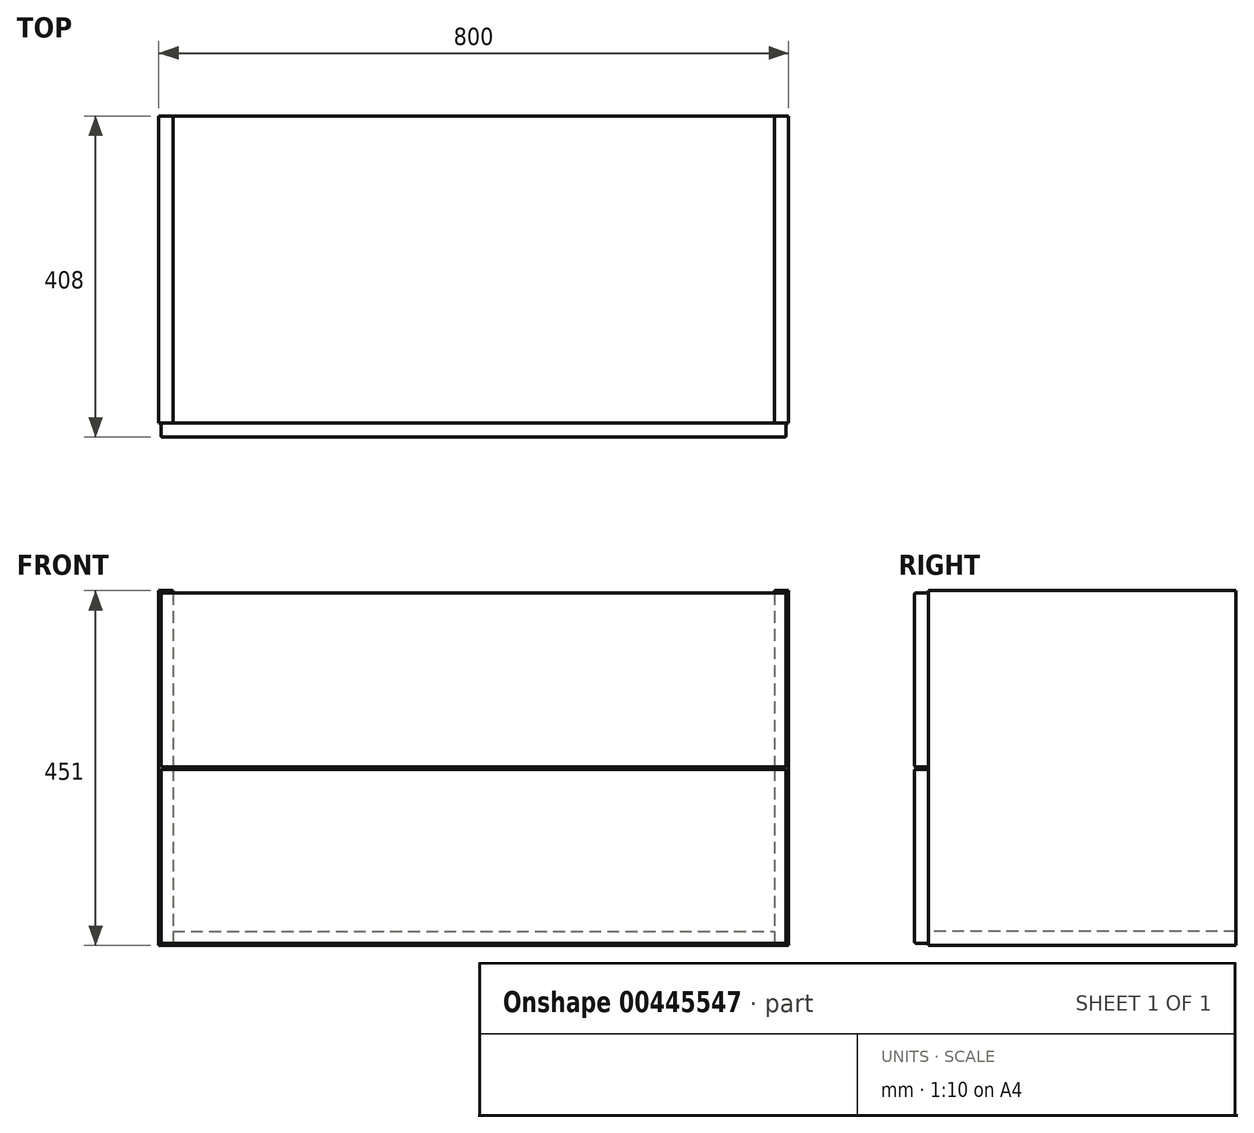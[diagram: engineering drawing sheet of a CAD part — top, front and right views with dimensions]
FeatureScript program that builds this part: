
annotation { "Feature Type Name" : "Feature", "Feature Type Description" : "" }
export const myFeature = defineFeature(function(context is Context, id is Id, definition is map)
    precondition{}
    {
        {
            var Q0;
            Q0=qCreatedBy(makeId("Front.planeOp"),FACE);
            var sketch = newSketch(context, id + "F0", { "sketchPlane" : qUnion([Q0])});
            skLineSegment(sketch, "E0.bottom", {"start": v(400, 225.5) * mm, "end": v(-400, 225.5) * mm});
            skLineSegment(sketch, "E0.top", {"start": v(400, -225.5) * mm, "end": v(-400, -225.5) * mm});
            skLineSegment(sketch, "E0.left", {"start": v(400, 225.5) * mm, "end": v(400, -225.5) * mm});
            skLineSegment(sketch, "E0.right", {"start": v(-400, 225.5) * mm, "end": v(-400, -225.5) * mm});
            skPoint(sketch, "E0.middle", {"position": v(0, 0) * mm});
            skLineSegment(sketch, "E1", {"start": v(-382, 225.5) * mm, "end": v(-382, -225.5) * mm});
            skLineSegment(sketch, "E2", {"start": v(382, 225.5) * mm, "end": v(382, -225.5) * mm});
            skLineSegment(sketch, "E3", {"start": v(-382, -207.5) * mm, "end": v(382, -207.5) * mm});
            skSolve(sketch);
        }
        {
            var Q0;
            {var subQ4=sQuery(id+"F0.wireOp",EDGE,"E0.right");Q0=makeQuery(id+"F0.imprint","IMPRINT",FACE,{"disambiguationData":[TD([[makeQuery(id+"F0.imprint","IMPRINT",EDGE,{"derivedFrom":subQ4}),1.0]])]});}
            var Q1;
            {var subQ0=sQuery(id+"F0.wireOp",EDGE,"E0.left");Q1=makeQuery(id+"F0.imprint","IMPRINT",FACE,{"disambiguationData":[TD([[makeQuery(id+"F0.imprint","IMPRINT",EDGE,{"derivedFrom":subQ0}),-1.0]])]});}
            extrude(context, id + "F1", {"entities" : qUnion([Q0, Q1]), "oppositeDirection" : true, "depth" : 390 * mm});
        }
        {
            var Q0;
            {var subQ5=sQuery(id+"F0.wireOp",EDGE,"E3");Q0=makeQuery(id+"F0.imprint","IMPRINT",FACE,{"disambiguationData":[TD([[makeQuery(id+"F0.imprint","IMPRINT",EDGE,{"derivedFrom":subQ5}),-1.0]])]});}
            extrude(context, id + "F2", {"entities" : qUnion([Q0]), "oppositeDirection" : true, "depth" : 390 * mm});
        }
        {
            var Q0;
            Q0=qCreatedBy(makeId("Front.planeOp"),FACE);
            var sketch = newSketch(context, id + "F3", { "sketchPlane" : qUnion([Q0])});
            skLineSegment(sketch, "E4.bottom", {"start": v(-397, -222.5) * mm, "end": v(397, -222.5) * mm});
            skLineSegment(sketch, "E4.top", {"start": v(-397, -1.5) * mm, "end": v(397, -1.5) * mm});
            skLineSegment(sketch, "E4.left", {"start": v(-397, -222.5) * mm, "end": v(-397, -1.5) * mm});
            skLineSegment(sketch, "E4.right", {"start": v(397, -222.5) * mm, "end": v(397, -1.5) * mm});
            skLineSegment(sketch, "E5.bottom", {"start": v(-397, 1.5) * mm, "end": v(397, 1.5) * mm});
            skLineSegment(sketch, "E5.top", {"start": v(-397, 222.5) * mm, "end": v(397, 222.5) * mm});
            skLineSegment(sketch, "E5.left", {"start": v(-397, 1.5) * mm, "end": v(-397, 222.5) * mm});
            skLineSegment(sketch, "E5.right", {"start": v(397, 1.5) * mm, "end": v(397, 222.5) * mm});
            skLineSegment(sketch, "E6", {"start": v(0, -222.5) * mm, "end": v(0, 220.3) * mm, "construction": true});
            skPoint(sketch, "E6.startSnap0", {"position": v(0, -222.5) * mm});
            skPoint(sketch, "E6.endSnap0", {"position": v(0, -222.5) * mm});
            skSolve(sketch);
        }
        {
            var Q0;
            Q0=makeQuery(id+"F3.imprint","IMPRINT",FACE,{"disambiguationData":[TD([[makeQuery(id+"F3.imprint","IMPRINT",EDGE,{"derivedFrom":sQuery(id+"F3.wireOp",EDGE,"E5.bottom")}),1.0]])]});
            var Q1;
            Q1=makeQuery(id+"F3.imprint","IMPRINT",FACE,{"disambiguationData":[TD([[makeQuery(id+"F3.imprint","IMPRINT",EDGE,{"derivedFrom":sQuery(id+"F3.wireOp",EDGE,"E4.bottom")}),1.0]])]});
            extrude(context, id + "F4", {"entities" : qUnion([Q0, Q1]), "depth" : 18 * mm});
        }
        {
            var Q0;
            Q0=makeQuery(id+"F4.opExtrude","CAP_FACE",FACE,{"disambiguationData":[OSD([sQuery(id+"F3.wireOp",EDGE,"E5.bottom"),sQuery(id+"F3.wireOp",EDGE,"E5.top"),sQuery(id+"F3.wireOp",EDGE,"E5.left"),sQuery(id+"F3.wireOp",EDGE,"E5.right")])],"isStart":false});
            var Q1;
            Q1=makeQuery(id+"F4.opExtrude","CAP_FACE",FACE,{"disambiguationData":[OSD([sQuery(id+"F3.wireOp",EDGE,"E4.bottom"),sQuery(id+"F3.wireOp",EDGE,"E4.top"),sQuery(id+"F3.wireOp",EDGE,"E4.left"),sQuery(id+"F3.wireOp",EDGE,"E4.right")])],"isStart":false});
            var Q2;
            Q2=makeQuery(id+"F4.opExtrude","SWEPT_EDGE",EDGE,{"disambiguationData":[OSD([sQuery(id+"F3.wireOp",EDGE,"E5.top"),sQuery(id+"F3.wireOp",EDGE,"E5.right")])]});
            var Q3;
            Q3=makeQuery(id+"F4.opExtrude","SWEPT_EDGE",EDGE,{"disambiguationData":[OSD([sQuery(id+"F3.wireOp",EDGE,"E5.top"),sQuery(id+"F3.wireOp",EDGE,"E5.left")])]});
            var Q4;
            Q4=makeQuery(id+"F4.opExtrude","SWEPT_EDGE",EDGE,{"disambiguationData":[OSD([sQuery(id+"F3.wireOp",EDGE,"E4.bottom"),sQuery(id+"F3.wireOp",EDGE,"E4.right")])]});
            var Q5;
            Q5=makeQuery(id+"F4.opExtrude","SWEPT_EDGE",EDGE,{"disambiguationData":[OSD([sQuery(id+"F3.wireOp",EDGE,"E4.top"),sQuery(id+"F3.wireOp",EDGE,"E4.right")])]});
            var Q6;
            Q6=makeQuery(id+"F4.opExtrude","SWEPT_EDGE",EDGE,{"disambiguationData":[OSD([sQuery(id+"F3.wireOp",EDGE,"E5.bottom"),sQuery(id+"F3.wireOp",EDGE,"E5.right")])]});
            var Q7;
            Q7=makeQuery(id+"F4.opExtrude","SWEPT_EDGE",EDGE,{"disambiguationData":[OSD([sQuery(id+"F3.wireOp",EDGE,"E4.bottom"),sQuery(id+"F3.wireOp",EDGE,"E4.left")])]});
            var Q8;
            Q8=makeQuery(id+"F4.opExtrude","SWEPT_EDGE",EDGE,{"disambiguationData":[OSD([sQuery(id+"F3.wireOp",EDGE,"E4.top"),sQuery(id+"F3.wireOp",EDGE,"E4.left")])]});
            fillet(context, id + "F5", {"entities" : qUnion([Q0, Q1, Q2, Q3, Q4, Q5, Q6, Q7, Q8]), "radius" : 2 * mm, "tangentPropagation" : true, "allowEdgeOverflow" : false});
        }
    });
